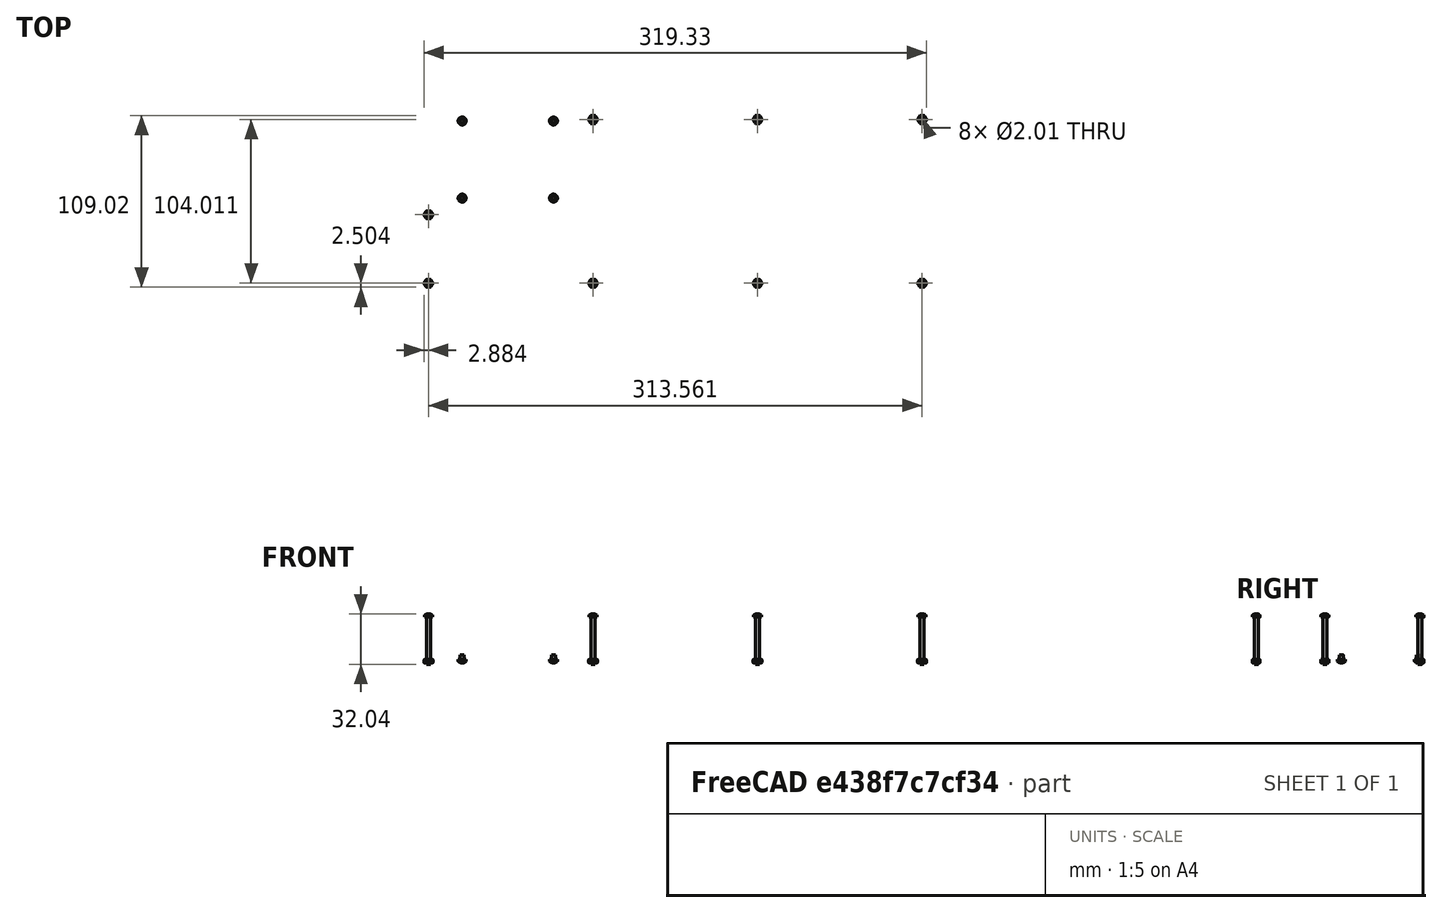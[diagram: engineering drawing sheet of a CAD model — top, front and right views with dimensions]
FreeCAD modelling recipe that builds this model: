
FCSTD DOCUMENT  (FreeCAD 0.19R24366 (Git))
Label: assembly
License: All rights reserved
LicenseURL: http://en.wikipedia.org/wiki/All_rights_reserved
objects: Part::FeaturePython×20, App::Link×17, App::DocumentObjectGroup×3, PartDesign::CoordinateSystem×1, App::FeaturePython×1, App::Part×1
note: 21 computed B-rep shape members (.brp) not serialized (recipe doc carries the construction recipe, not evaluated geometry)
EXTERNAL_REF file=../bottom_layer/bottom_layer.FCStd obj=bottom_layer_lcs
EXTERNAL_REF file=../bottom_layer/bottom_layer.FCStd obj=Part
EXTERNAL_REF file=../lower_layer/lower_layer.FCStd obj=top_left_lcs_closed_layer
EXTERNAL_REF file=../master.FCStd obj=Spreadsheet
EXTERNAL_REF file=../lower_layer/lower_layer.FCStd obj=Part
EXTERNAL_REF file=../top_layer/top_layer.FCStd obj=top_left_lcs_closed_layer
EXTERNAL_REF file=../top_layer/top_layer.FCStd obj=Part
EXTERNAL_REF file=../switch_layer/switch_layer.FCStd obj=top_left_LCS_switch_layer
EXTERNAL_REF file=../switch_layer/switch_layer.FCStd obj=Part
EXTERNAL_REF file=../raspberry_pi/raspberry_pi_4.FCStd obj=LCS_0
EXTERNAL_REF file=../raspberry_pi/raspberry_pi_4.FCStd obj=raspberry_pi_4
EXTERNAL_REF file=../hyperpixel/hyperpixel.FCStd obj=LCS_0
EXTERNAL_REF file=../hyperpixel/hyperpixel.FCStd obj=Part
EXTERNAL_REF file=../switch_layer/switch_layer.FCStd obj=Body
EXTERNAL_REF file=../bottom_layer/bottom_layer.FCStd obj=Body
EXTERNAL_REF file=../pcb/pcb.FCStd obj=pcb_lcs
EXTERNAL_REF file=../pcb/pcb.FCStd obj=Part
EXTERNAL_REF file=../keycaps/keycaps.FCStd obj=keycaps_lcs
EXTERNAL_REF file=../keycaps/keycaps.FCStd obj=Part
EXTERNAL_REF file=../encoder_knob/encoder_knob.FCStd obj=encoder_knob_lcs
EXTERNAL_REF file=../pcb/pcb.FCStd obj=encoder_1_lcs
EXTERNAL_REF file=../encoder_knob/encoder_knob.FCStd obj=Part
EXTERNAL_REF file=../pcb/pcb.FCStd obj=encoder_2_lcs
EXTERNAL_REF file=../pcb/pcb.FCStd obj=encoder_3_lcs
EXTERNAL_REF file=../pcb/pcb.FCStd obj=encoder_4_lcs

FEATURE [App::DocumentObjectGroup] Parts
FEATURE [PartDesign::CoordinateSystem] LCS_Origin
  AttacherType = Attacher::AttachEngine3D
  MapMode = 2
  Support = -> [X_Axis]
FEATURE [App::FeaturePython] Variables  # WARN: FeaturePython — macro-defined, semantics opaque (R4)
  Type = App::PropertyContainer
FEATURE [App::DocumentObjectGroup] Constraints
FEATURE [App::DocumentObjectGroup] Configurations
FEATURE [App::Link] bottom_layer_part
  AttachedBy = #bottom_layer_lcs
  AttachedTo = Parent Assembly#LCS_Origin
  ElementCount = 0
  LinkPlacement = pos=(0,0,-3) rot=(0,0,1;0rad)
  LinkTransform = false
  Placement = pos=(0,0,-3) rot=(0,0,1;0rad)
  Scale = 1
  ScaleVector = (1,1,1)
  ShowElement = true
  SolverId = Placement::ExpressionEngine
  expr: Placement = LCS_Origin.Placement * AttachmentOffset * bottom_layer#bottom_layer_lcs.Placement ^ -1
FEATURE [App::Link] lower_layer_part_1
  AttachedBy = #top_left_lcs_closed_layer
  AttachedTo = bottom_layer_part#bottom_layer_lcs
  AttachmentOffset = pos=(0,0,3) rot=(0,0,1;0rad)
  ElementCount = 0
  LinkTransform = false
  Scale = 1
  ScaleVector = (1,1,1)
  ShowElement = true
  SolverId = Placement::ExpressionEngine
  expr: Placement = bottom_layer_part.Placement * bottom_layer#bottom_layer_lcs.Placement * AttachmentOffset * lower_layer#top_left_lcs_closed_layer.Placement ^ -1
  expr: .AttachmentOffset.Base.z = <<master>>#<<inputs>>.lower_layer_thickness
FEATURE [App::Link] lower_layer_part_2
  AttachedBy = #top_left_lcs_closed_layer
  AttachedTo = lower_layer_part_1#top_left_lcs_closed_layer
  AttachmentOffset = pos=(0,0,3) rot=(0,0,1;0rad)
  ElementCount = 0
  LinkPlacement = pos=(0,0,3) rot=(0,0,1;0rad)
  LinkTransform = false
  Placement = pos=(0,0,3) rot=(0,0,1;0rad)
  Scale = 1
  ScaleVector = (1,1,1)
  ShowElement = true
  SolverId = Placement::ExpressionEngine
  expr: Placement = lower_layer_part_1.Placement * lower_layer#top_left_lcs_closed_layer.Placement * AttachmentOffset * lower_layer#top_left_lcs_closed_layer.Placement ^ -1
  expr: .AttachmentOffset.Base.z = <<master>>#<<inputs>>.lower_layer_thickness
FEATURE [App::Link] lower_layer_part_3
  AttachedBy = #top_left_lcs_closed_layer
  AttachedTo = lower_layer_part_2#top_left_lcs_closed_layer
  AttachmentOffset = pos=(0,0,3) rot=(0,0,1;0rad)
  ElementCount = 0
  LinkPlacement = pos=(0,0,6) rot=(0,0,1;0rad)
  LinkTransform = false
  Placement = pos=(0,0,6) rot=(0,0,1;0rad)
  Scale = 1
  ScaleVector = (1,1,1)
  ShowElement = true
  SolverId = Placement::ExpressionEngine
  expr: Placement = lower_layer_part_2.Placement * lower_layer#top_left_lcs_closed_layer.Placement * AttachmentOffset * lower_layer#top_left_lcs_closed_layer.Placement ^ -1
  expr: .AttachmentOffset.Base.z = <<master>>#<<inputs>>.lower_layer_thickness
FEATURE [App::Link] lower_layer_part_4
  AttachedBy = #top_left_lcs_closed_layer
  AttachedTo = lower_layer_part_3#top_left_lcs_closed_layer
  AttachmentOffset = pos=(0,0,3) rot=(0,0,1;0rad)
  ElementCount = 0
  LinkPlacement = pos=(0,0,9) rot=(0,0,1;0rad)
  LinkTransform = false
  Placement = pos=(0,0,9) rot=(0,0,1;0rad)
  Scale = 1
  ScaleVector = (1,1,1)
  ShowElement = true
  SolverId = Placement::ExpressionEngine
  expr: Placement = lower_layer_part_3.Placement * lower_layer#top_left_lcs_closed_layer.Placement * AttachmentOffset * lower_layer#top_left_lcs_closed_layer.Placement ^ -1
  expr: .AttachmentOffset.Base.z = <<master>>#<<inputs>>.lower_layer_thickness
FEATURE [App::Link] lower_layer_part_5
  AttachedBy = #top_left_lcs_closed_layer
  AttachedTo = lower_layer_part_4#top_left_lcs_closed_layer
  AttachmentOffset = pos=(0,0,3) rot=(0,0,1;0rad)
  ElementCount = 0
  LinkPlacement = pos=(0,0,12) rot=(0,0,1;0rad)
  LinkTransform = false
  Placement = pos=(0,0,12) rot=(0,0,1;0rad)
  Scale = 1
  ScaleVector = (1,1,1)
  ShowElement = true
  SolverId = Placement::ExpressionEngine
  expr: Placement = lower_layer_part_4.Placement * lower_layer#top_left_lcs_closed_layer.Placement * AttachmentOffset * lower_layer#top_left_lcs_closed_layer.Placement ^ -1
  expr: .AttachmentOffset.Base.z = <<master>>#<<inputs>>.lower_layer_thickness
FEATURE [App::Link] top_layer_part_1
  AttachedBy = #top_left_lcs_closed_layer
  AttachedTo = lower_layer_part_5#top_left_lcs_closed_layer
  AttachmentOffset = pos=(0,0,3) rot=(0,0,1;0rad)
  ElementCount = 0
  LinkPlacement = pos=(0,0,15) rot=(0,0,1;0rad)
  LinkTransform = false
  Placement = pos=(0,0,15) rot=(0,0,1;0rad)
  Scale = 1
  ScaleVector = (1,1,1)
  ShowElement = true
  SolverId = Placement::ExpressionEngine
  expr: Placement = lower_layer_part_5.Placement * lower_layer#top_left_lcs_closed_layer.Placement * AttachmentOffset * top_layer#top_left_lcs_closed_layer.Placement ^ -1
  expr: .AttachmentOffset.Base.z = <<master>>#<<inputs>>.top_layer_thickness
FEATURE [App::Link] top_layer_part_2
  AttachedBy = #top_left_lcs_closed_layer
  AttachedTo = top_layer_part_1#top_left_lcs_closed_layer
  AttachmentOffset = pos=(0,0,3) rot=(0,0,1;0rad)
  ElementCount = 0
  LinkPlacement = pos=(0,0,18) rot=(0,0,1;0rad)
  LinkTransform = false
  Placement = pos=(0,0,18) rot=(0,0,1;0rad)
  Scale = 1
  ScaleVector = (1,1,1)
  ShowElement = true
  SolverId = Placement::ExpressionEngine
  expr: Placement = top_layer_part_1.Placement * top_layer#top_left_lcs_closed_layer.Placement * AttachmentOffset * top_layer#top_left_lcs_closed_layer.Placement ^ -1
  expr: .AttachmentOffset.Base.z = <<master>>#<<inputs>>.top_layer_thickness
FEATURE [App::Link] switch_layer_part
  AttachedBy = #top_left_LCS_switch_layer
  AttachedTo = top_layer_part_2#top_left_lcs_closed_layer
  AttachmentOffset = pos=(0,0,3) rot=(0,0,1;0rad)
  ElementCount = 0
  LinkPlacement = pos=(0,0,21) rot=(0,0,1;0rad)
  LinkTransform = false
  Placement = pos=(0,0,21) rot=(0,0,1;0rad)
  Scale = 1
  ScaleVector = (1,1,1)
  ShowElement = true
  SolverId = Placement::ExpressionEngine
  expr: Placement = top_layer_part_2.Placement * top_layer#top_left_lcs_closed_layer.Placement * AttachmentOffset * switch_layer#top_left_LCS_switch_layer.Placement ^ -1
  expr: .AttachmentOffset.Base.z = <<master>>#<<inputs>>.switch_layer_thickness
FEATURE [App::Link] raspberry_pi_4_part
  AttachedBy = #LCS_0
  AttachedTo = bottom_layer_part#bottom_layer_lcs
  AttachmentOffset = pos=(26.52,-11.52,2.8) rot=(0,0,1;0rad)
  ElementCount = 0
  LinkPlacement = pos=(26.52,-11.52,2.8) rot=(0,0,1;0rad)
  LinkTransform = false
  Placement = pos=(26.52,-11.52,2.8) rot=(0,0,1;0rad)
  Scale = 1
  ScaleVector = (1,1,1)
  ShowElement = true
  SolverId = Placement::ExpressionEngine
  expr: Placement = bottom_layer_part.Placement * bottom_layer#bottom_layer_lcs.Placement * AttachmentOffset * raspberry_pi_4#LCS_0.Placement ^ -1
FEATURE [App::Link] hyperpixel_part
  AttachedBy = #LCS_0
  AttachedTo = raspberry_pi_4_part#LCS_0
  AttachmentOffset = pos=(54,29,17.8) rot=(0,0,1;0rad)
  ElementCount = 0
  LinkPlacement = pos=(80.52,17.48,20.6) rot=(0,0,1;0rad)
  LinkTransform = false
  Placement = pos=(80.52,17.48,20.6) rot=(0,0,1;0rad)
  Scale = 1
  ScaleVector = (1,1,1)
  ShowElement = true
  SolverId = Placement::ExpressionEngine
  expr: Placement = raspberry_pi_4_part.Placement * raspberry_pi_4#LCS_0.Placement * AttachmentOffset * hyperpixel#LCS_0.Placement ^ -1
FEATURE [Part::FeaturePython] Screw  label="M2.5x30-Screw"  # WARN: FeaturePython — macro-defined, semantics opaque (R4)
  Placement = pos=(299.656,13.9055,24) rot=(0,0,1;0rad)
  diameter = 3
  invert = false
  length = 11
  lengthCustom = 30
  matchOuter = true
  offset = 21
  thread = false
  type = 35
FEATURE [Part::FeaturePython] Screw001  label="M2.5x30-Screw035"  # WARN: FeaturePython — macro-defined, semantics opaque (R4)
  Placement = pos=(195.135,13.9055,24) rot=(0,0,1;0rad)
  diameter = 3
  invert = false
  length = 11
  lengthCustom = 30
  matchOuter = true
  offset = 21
  thread = false
  type = 35
FEATURE [Part::FeaturePython] Screw002  label="M2.5x30-Screw036"  # WARN: FeaturePython — macro-defined, semantics opaque (R4)
  Placement = pos=(90.6148,13.9055,24) rot=(0,0,1;0rad)
  diameter = 3
  invert = false
  length = 11
  lengthCustom = 30
  matchOuter = true
  offset = 21
  thread = false
  type = 35
FEATURE [Part::FeaturePython] Screw003  label="M2.5x30-Screw037"  # WARN: FeaturePython — macro-defined, semantics opaque (R4)
  Placement = pos=(299.656,-90.1055,24) rot=(0,0,1;0rad)
  diameter = 3
  invert = false
  length = 11
  lengthCustom = 30
  matchOuter = true
  offset = 21
  thread = false
  type = 35
FEATURE [Part::FeaturePython] Screw004  label="M2.5x30-Screw038"  # WARN: FeaturePython — macro-defined, semantics opaque (R4)
  Placement = pos=(195.135,-90.1055,24) rot=(0,0,1;0rad)
  diameter = 3
  invert = false
  length = 11
  lengthCustom = 30
  matchOuter = true
  offset = 21
  thread = false
  type = 35
FEATURE [Part::FeaturePython] Screw005  label="M2.5x30-Screw039"  # WARN: FeaturePython — macro-defined, semantics opaque (R4)
  Placement = pos=(90.6148,-90.1055,24) rot=(0,0,1;0rad)
  diameter = 3
  invert = false
  length = 11
  lengthCustom = 30
  matchOuter = true
  offset = 21
  thread = false
  type = 35
FEATURE [Part::FeaturePython] Screw006  label="M2.5x30-Screw040"  # WARN: FeaturePython — macro-defined, semantics opaque (R4)
  Placement = pos=(-13.9055,-90.1055,24) rot=(0,0,1;0rad)
  diameter = 3
  invert = false
  length = 11
  lengthCustom = 30
  matchOuter = true
  offset = 21
  thread = false
  type = 35
FEATURE [Part::FeaturePython] Screw007  label="M2.5x30-Screw041"  # WARN: FeaturePython — macro-defined, semantics opaque (R4)
  Placement = pos=(-13.9055,-46.578,24) rot=(0,0,1;0rad)
  diameter = 3
  invert = false
  length = 11
  lengthCustom = 30
  matchOuter = true
  offset = 21
  thread = false
  type = 35
FEATURE [Part::FeaturePython] Nut  label="M2.5-Nut"  # WARN: FeaturePython — macro-defined, semantics opaque (R4)
  Placement = pos=(-13.9055,-90.1055,-3) rot=(-1,0,0;3.14159rad)
  diameter = 3
  invert = true
  matchOuter = true
  offset = 3
  thread = false
  type = 7
FEATURE [Part::FeaturePython] Nut001  label="M2.5-Nut092"  # WARN: FeaturePython — macro-defined, semantics opaque (R4)
  Placement = pos=(90.6148,-90.1055,-3) rot=(-1,0,0;3.14159rad)
  diameter = 3
  invert = true
  matchOuter = true
  offset = 3
  thread = false
  type = 7
FEATURE [Part::FeaturePython] Nut002  label="M2.5-Nut093"  # WARN: FeaturePython — macro-defined, semantics opaque (R4)
  Placement = pos=(195.135,-90.1055,-3) rot=(-1,0,0;3.14159rad)
  diameter = 3
  invert = true
  matchOuter = true
  offset = 3
  thread = false
  type = 7
FEATURE [Part::FeaturePython] Nut003  label="M2.5-Nut094"  # WARN: FeaturePython — macro-defined, semantics opaque (R4)
  Placement = pos=(299.656,-90.1055,-3) rot=(-1,0,0;3.14159rad)
  diameter = 3
  invert = true
  matchOuter = true
  offset = 3
  thread = false
  type = 7
FEATURE [Part::FeaturePython] Nut004  label="M2.5-Nut095"  # WARN: FeaturePython — macro-defined, semantics opaque (R4)
  Placement = pos=(299.656,13.9055,-3) rot=(-1,0,0;3.14159rad)
  diameter = 3
  invert = true
  matchOuter = true
  offset = 3
  thread = false
  type = 7
FEATURE [Part::FeaturePython] Nut005  label="M2.5-Nut096"  # WARN: FeaturePython — macro-defined, semantics opaque (R4)
  Placement = pos=(195.135,13.9055,-3) rot=(-1,0,0;3.14159rad)
  diameter = 3
  invert = true
  matchOuter = true
  offset = 3
  thread = false
  type = 7
FEATURE [Part::FeaturePython] Nut006  label="M2.5-Nut097"  # WARN: FeaturePython — macro-defined, semantics opaque (R4)
  Placement = pos=(-13.9055,-46.578,-3) rot=(-1,0,0;3.14159rad)
  diameter = 3
  invert = true
  matchOuter = true
  offset = 3
  thread = false
  type = 7
FEATURE [Part::FeaturePython] Nut007  label="M2.5-Nut098"  # WARN: FeaturePython — macro-defined, semantics opaque (R4)
  Placement = pos=(90.6148,13.9055,-3) rot=(-1,0,0;3.14159rad)
  diameter = 3
  invert = true
  matchOuter = true
  offset = 3
  thread = false
  type = 7
FEATURE [Part::FeaturePython] Screw012  label="M2.5x3-Screw"  # WARN: FeaturePython — macro-defined, semantics opaque (R4)
  Placement = pos=(65.5225,12.9775,-3) rot=(-1,0,0;3.14159rad)
  diameter = 3
  invert = true
  length = 0
  lengthCustom = 3
  matchOuter = true
  offset = 3
  thread = false
  type = 35
FEATURE [Part::FeaturePython] Screw013  label="M2.5x3-Screw057"  # WARN: FeaturePython — macro-defined, semantics opaque (R4)
  Placement = pos=(7.5225,12.9775,-3) rot=(-1,0,0;3.14159rad)
  diameter = 3
  invert = true
  length = 0
  lengthCustom = 3
  matchOuter = true
  offset = 3
  thread = false
  type = 35
FEATURE [Part::FeaturePython] Screw014  label="M2.5x3-Screw058"  # WARN: FeaturePython — macro-defined, semantics opaque (R4)
  Placement = pos=(7.5225,-36.0225,-3) rot=(-1,0,0;3.14159rad)
  diameter = 3
  invert = true
  length = 0
  lengthCustom = 3
  matchOuter = true
  offset = 3
  thread = false
  type = 35
FEATURE [Part::FeaturePython] Screw015  label="M2.5x3-Screw059"  # WARN: FeaturePython — macro-defined, semantics opaque (R4)
  Placement = pos=(65.5225,-36.0225,-3) rot=(-1,0,0;3.14159rad)
  diameter = 3
  invert = true
  length = 0
  lengthCustom = 3
  matchOuter = true
  offset = 3
  thread = false
  type = 35
FEATURE [App::Link] pcb_part
  AttachedBy = #pcb_lcs
  AttachedTo = switch_layer_part#top_left_LCS_switch_layer
  AttachmentOffset = pos=(0,0,-5) rot=(0,0,1;0rad)
  ElementCount = 0
  LinkPlacement = pos=(0,0,17.4) rot=(0,0,1;0rad)
  LinkTransform = false
  Placement = pos=(0,0,17.4) rot=(0,0,1;0rad)
  Scale = 1
  ScaleVector = (1,1,1)
  ShowElement = true
  SolverId = Placement::ExpressionEngine
  expr: Placement = switch_layer_part.Placement * switch_layer#top_left_LCS_switch_layer.Placement * AttachmentOffset * pcb#pcb_lcs.Placement ^ -1
FEATURE [App::Link] keycaps_part
  AttachedBy = #keycaps_lcs
  AttachedTo = switch_layer_part#top_left_LCS_switch_layer
  AttachmentOffset = pos=(0,0,4) rot=(0,0,1;0rad)
  ElementCount = 0
  LinkPlacement = pos=(0,0,28) rot=(0,0,1;0rad)
  LinkTransform = false
  Placement = pos=(0,0,28) rot=(0,0,1;0rad)
  Scale = 1
  ScaleVector = (1,1,1)
  ShowElement = true
  SolverId = Placement::ExpressionEngine
  expr: Placement = switch_layer_part.Placement * switch_layer#top_left_LCS_switch_layer.Placement * AttachmentOffset * keycaps#keycaps_lcs.Placement ^ -1
FEATURE [App::Link] encoder_knob_part
  AttachedBy = #encoder_knob_lcs
  AttachedTo = pcb_part#encoder_1_lcs
  AttachmentOffset = pos=(0,0,-7) rot=(-0.707107,-0.707107,0;3.14159rad)
  ElementCount = 0
  LinkPlacement = pos=(200.025,-0.1905,25.5325) rot=(0,0,1;0rad)
  LinkTransform = false
  Placement = pos=(200.025,-0.1905,25.5325) rot=(0,0,1;0rad)
  Scale = 1
  ScaleVector = (1,1,1)
  ShowElement = true
  SolverId = Placement::ExpressionEngine
  expr: Placement = pcb_part.Placement * pcb#encoder_1_lcs.Placement * AttachmentOffset * encoder_knob#encoder_knob_lcs.Placement ^ -1
FEATURE [App::Link] encoder_knob_part_2
  AttachedBy = #encoder_knob_lcs
  AttachedTo = pcb_part#encoder_2_lcs
  AttachmentOffset = pos=(0,0,-7) rot=(-0.707107,-0.707107,0;3.14159rad)
  ElementCount = 0
  LinkPlacement = pos=(228.6,-3.2382e-12,25.5325) rot=(0,0,1;0rad)
  LinkTransform = false
  Placement = pos=(228.6,-3.2382e-12,25.5325) rot=(0,0,1;0rad)
  Scale = 1
  ScaleVector = (1,1,1)
  ShowElement = true
  SolverId = Placement::ExpressionEngine
  expr: Placement = pcb_part.Placement * pcb#encoder_2_lcs.Placement * AttachmentOffset * encoder_knob#encoder_knob_lcs.Placement ^ -1
FEATURE [App::Link] encoder_knob_part_3
  AttachedBy = #encoder_knob_lcs
  AttachedTo = pcb_part#encoder_3_lcs
  AttachmentOffset = pos=(0,0,-7) rot=(-0.707107,-0.707107,0;3.14159rad)
  ElementCount = 0
  LinkPlacement = pos=(257.175,-3.2382e-12,25.5325) rot=(0,0,1;0rad)
  LinkTransform = false
  Placement = pos=(257.175,-3.2382e-12,25.5325) rot=(0,0,1;0rad)
  Scale = 1
  ScaleVector = (1,1,1)
  ShowElement = true
  SolverId = Placement::ExpressionEngine
  expr: Placement = pcb_part.Placement * pcb#encoder_3_lcs.Placement * AttachmentOffset * encoder_knob#encoder_knob_lcs.Placement ^ -1
FEATURE [App::Link] encoder_knob_part_4
  AttachedBy = #encoder_knob_lcs
  AttachedTo = pcb_part#encoder_4_lcs
  AttachmentOffset = pos=(0,0,-7) rot=(-0.707107,-0.707107,0;3.14159rad)
  ElementCount = 0
  LinkPlacement = pos=(285.75,-3.2382e-12,25.5325) rot=(0,0,1;0rad)
  LinkTransform = false
  Placement = pos=(285.75,-3.2382e-12,25.5325) rot=(0,0,1;0rad)
  Scale = 1
  ScaleVector = (1,1,1)
  ShowElement = true
  SolverId = Placement::ExpressionEngine
  expr: Placement = pcb_part.Placement * pcb#encoder_4_lcs.Placement * AttachmentOffset * encoder_knob#encoder_knob_lcs.Placement ^ -1
FEATURE [App::Part] Assembly
  AssemblyType = Part::Link
  Group = -> [LCS_Origin,Variables,Constraints,Configurations,bottom_layer_part,lower_layer_part_1,lower_layer_part_2,lower_layer_part_3,lower_layer_part_4,lower_layer_part_5,top_layer_part_1,top_layer_part_2,switch_layer_part,raspberry_pi_4_part,hyperpixel_part,pcb_part,keycaps_part,encoder_knob_part,encoder_knob_part_2,encoder_knob_part_3,encoder_knob_part_4]
  Origin = -> Origin
  Type = Assembly
